# Revit family: Sarlam_Lighting_Bulkhead_Chartres_Infini_T2_Vandal_resistant_Diam_435mm_3000Lm
name_source: partatom
category: Luminaires
units: mm (PartAtom-declared; Revit-internal decimal feet)

## family parameters
Cote de connecteur circulaire = Utiliser le diamètre
Couper avec des vides une fois chargée = Non
Hôte = Face
Partagée = Non
Point de calcul de pièce = Non
Source d'éclairage = Oui
Type d'élément = Normal

## types (8) — shared parameters
Angle de l'inclinaison = 0.00°
Antivandale Formes 2-4-7 = Oui
Built-in width = 435 mm  [stored 1.42717 ft]
Colour rendering index CRI = 80-89
Colour temperature K MAX = 4000
Colour temperature K MIN = 4000
Effective luminous flux lm = 3000
Elévation par défaut = 2500 mm  [stored 8.2021 ft]
Emettre la visibilité des formes dans le rendu = Non
Emettre à partir du diamètre du cercle = 300 mm
Fabricant = LEGRAND
Fichier de distribution photométrique = SL532009.ies
Filtre de couleur = 16777215
General Conditions of Use = https://export.legrand.com
Gradation des changements de température de couleur de lampe = <Aucun>
Height/depth = 90 mm  [stored 0.295276 ft]
Lamp holder = None
Lamp power at multiwatt = 21/39W
Lamp type = LED not exchangeable
Length = 435 mm  [stored 1.42717 ft]
Light sharing = Symmetric
Material housing = Plastique
Nominal voltage (Un) V MAX = 253
Nominal voltage (Un) V MIN = 207
Outer diameter = 435 mm  [stored 1.42717 ft]
Protection Class = II
Radiation angle = Open beam
Suitable for built-in mounting = Non
Suitable for ceiling mounting = Oui
Suitable for surface mounting = Oui
Suitable for suspended mounting = Non
Suitable for wall mounting = Oui
Type of control gear = LED operating device current-controlled
URL = http://www.legrandoc.com
Voltage type = AC
Width = 435 mm  [stored 1.42717 ft]
zero-valued in all types: Built-in diameter, Built-in height/depth, Built-in length, Nominal current mA MAX, Nominal current mA MIN, System power W

## per-type parameters (varying)
| type | Colour housing | Degree of protection (IP) | Description | Detection area | Impact strength (IK) | Modèle | Type of dimming | With light sensor | With movement sensor |
| ON/OFF WHITE | LEGRAND - White | IP55 | CHARTRES INFINI 3000LM 4000K AV ON/OFF WHITE |  | IK10 | SL-532015 | Not dimmable | Non | Non |
| ON/OFF ANTHRACITE | LEGRAND - Anthracite | IP55 | CHARTRES INFINI 3000LM 4000K AV ON/OFF BLACK |  | IK10 | SL-532016 | Not dimmable | Non | Non |
| ON/OFF GREY METAL | LEGRAND - Grey | IP55 | CHARTRES INFINI 3000LM 4000K AV ON/OFF SILVER |  | IK10 | SL-532017 | Not dimmable | Non | Non |
| With microwave sensor WHITE | LEGRAND - White | IP55 | CHARTRES INFINI 3000LM 4000K  AV DETECTION HF WHITE | Detection at 2,5m high Ceiling: Ø6m max Wall: Ellipse 16*17m | IK10 | SL-532055 | Other | Oui | Oui |
| With microwave sensor ANTHRACITE | LEGRAND - Anthracite | IP55 | CHARTRES INFINI 3000LM 4000K  AV DETECTION HF BLACK | Detection at 2,5m high Ceiling: Ø6m max Wall: Ellipse 16*17m | IK10 | SL-532056 | Other | Oui | Oui |
| With microwave sensor GREY METAL | LEGRAND - Grey | IP55 | CHARTRES INFINI 3000LM 4000K  AV DETECTION HF SILVER | Detection at 2,5m high Ceiling: Ø6m max Wall: Ellipse 16*17m | IK10 | SL-532057 | Other | Oui | Oui |
| Vandal resistant-ON/OFF | LEGRAND - White | IP66 | CHARTRES INFINI 3000LM 4000K SOLIROC ON/OFF WHITE |  | >IK10 | SL-532098 | Not dimmable | Non | Non |
| Vandal resistant - With microwave sensor | LEGRAND - White | IP66 | CHARTRES INFINI 3000LM 4000K  SOLIROC DETECTION HF WHITE | Detection at 2,5m high Ceiling: Ø6m max Wall: Ellipse 16*17m | >IK10 | SL-532099 | Other | Oui | Oui |

note: [stored X ft] marks values corroborated as IEEE doubles in the binary element streams (Revit-internal decimal feet)

## geometry (parser evidence)
native form markers: Blend x10
no freeform markers — native parametric forms only
